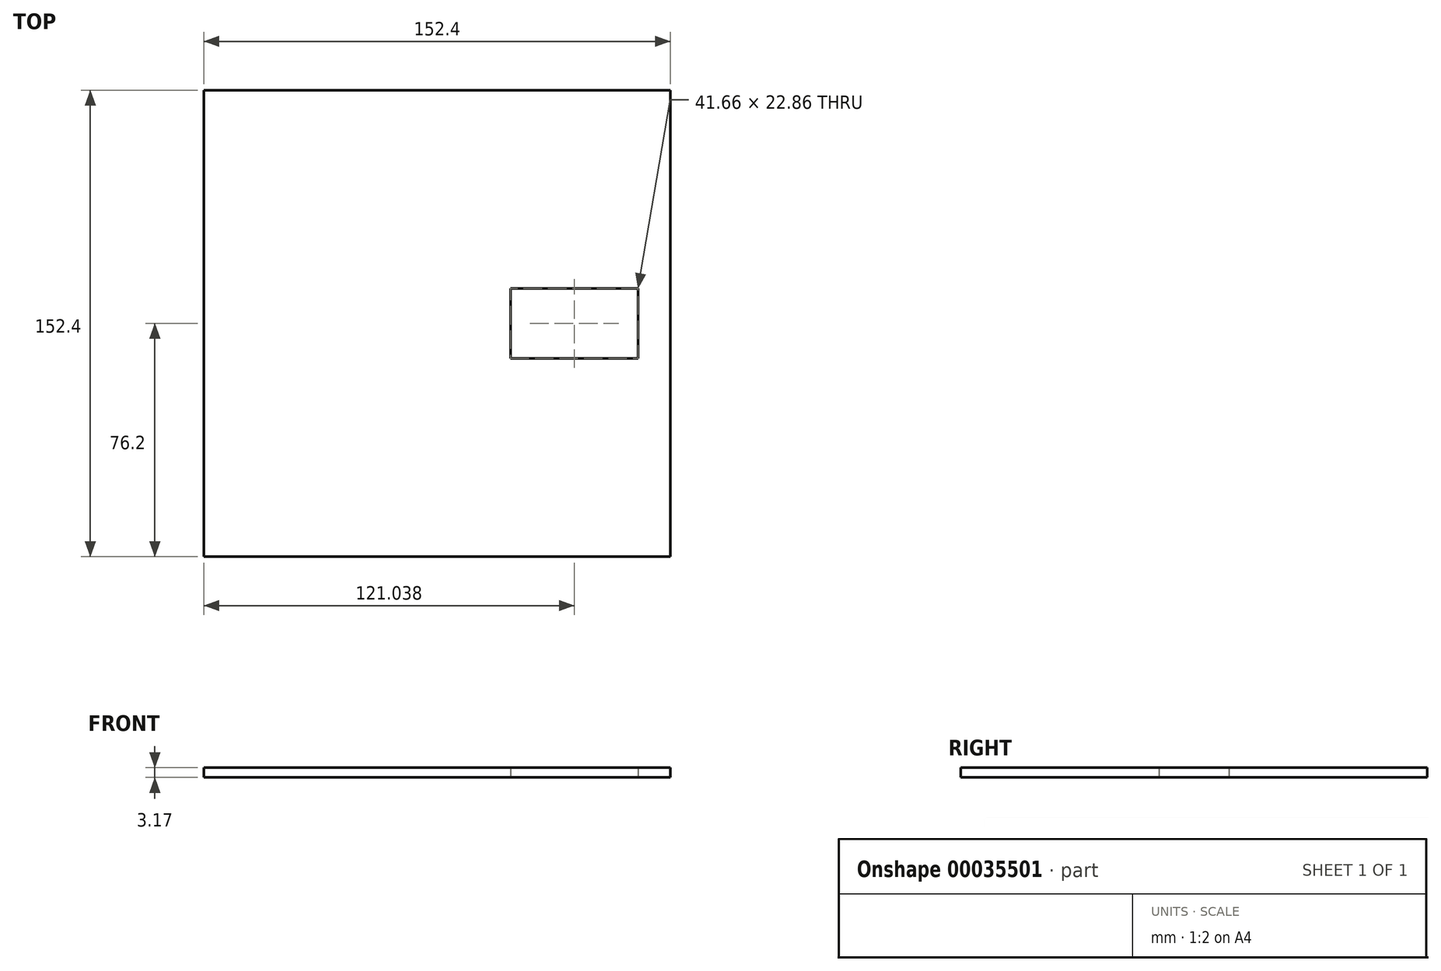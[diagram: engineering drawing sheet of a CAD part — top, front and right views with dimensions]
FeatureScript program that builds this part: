
annotation { "Feature Type Name" : "Feature", "Feature Type Description" : "" }
export const myFeature = defineFeature(function(context is Context, id is Id, definition is map)
    precondition{}
    {
        {
            var Q0;
            Q0=qCreatedBy(makeId("Top.planeOp"),FACE);
            var sketch = newSketch(context, id + "F0", { "sketchPlane" : qUnion([Q0])});
            skLineSegment(sketch, "E0.rect.bottom", {"start": v(76.2, 76.2) * mm, "end": v(-76.2, 76.2) * mm});
            skLineSegment(sketch, "E0.rect.top", {"start": v(76.2, -76.2) * mm, "end": v(-76.2, -76.2) * mm});
            skLineSegment(sketch, "E0.rect.left", {"start": v(76.2, 76.2) * mm, "end": v(76.2, -76.2) * mm});
            skLineSegment(sketch, "E0.rect.right", {"start": v(-76.2, 76.2) * mm, "end": v(-76.2, -76.2) * mm});
            skPoint(sketch, "E0.rect.middle", {"position": v(0, 0) * mm});
            skSolve(sketch);
        }
        {
            var Q0;
            Q0=makeQuery(id+"F0.imprint","IMPRINT",FACE,{"disambiguationData":[TD([[makeQuery(id+"F0.imprint","IMPRINT",EDGE,{"derivedFrom":sQuery(id+"F0.wireOp",EDGE,"E0.rect.bottom")}),1.0]])]});
            var sketch = newSketch(context, id + "F1", { "sketchPlane" : qUnion([Q0])});
            skLineSegment(sketch, "E1", {"start": v(-183.2, 0) * mm, "end": v(244.73, 0) * mm, "construction": true});
            skLineSegment(sketch, "E2.rect.bottom", {"start": v(24, 11.43) * mm, "end": v(65.67, 11.43) * mm});
            skLineSegment(sketch, "E2.rect.top", {"start": v(24, -11.43) * mm, "end": v(65.67, -11.43) * mm});
            skLineSegment(sketch, "E2.rect.left", {"start": v(24, 11.43) * mm, "end": v(24, -11.43) * mm});
            skLineSegment(sketch, "E2.rect.right", {"start": v(65.67, 11.43) * mm, "end": v(65.67, -11.43) * mm});
            skPoint(sketch, "E2.rect.middle", {"position": v(44.84, 0) * mm});
            skSolve(sketch);
        }
        {
            var Q0;
            Q0=makeQuery(id+"F1.imprint","IMPRINT",FACE,{"disambiguationData":[TD([[makeQuery(id+"F1.imprint","IMPRINT",EDGE,{"derivedFrom":sQuery(id+"F1.wireOp",EDGE,"E2.rect.bottom")}),1.0]])]});
            extrude(context, id + "F2", {"entities" : qUnion([Q0]), "depth" : 3.17 * mm});
        }
    });
